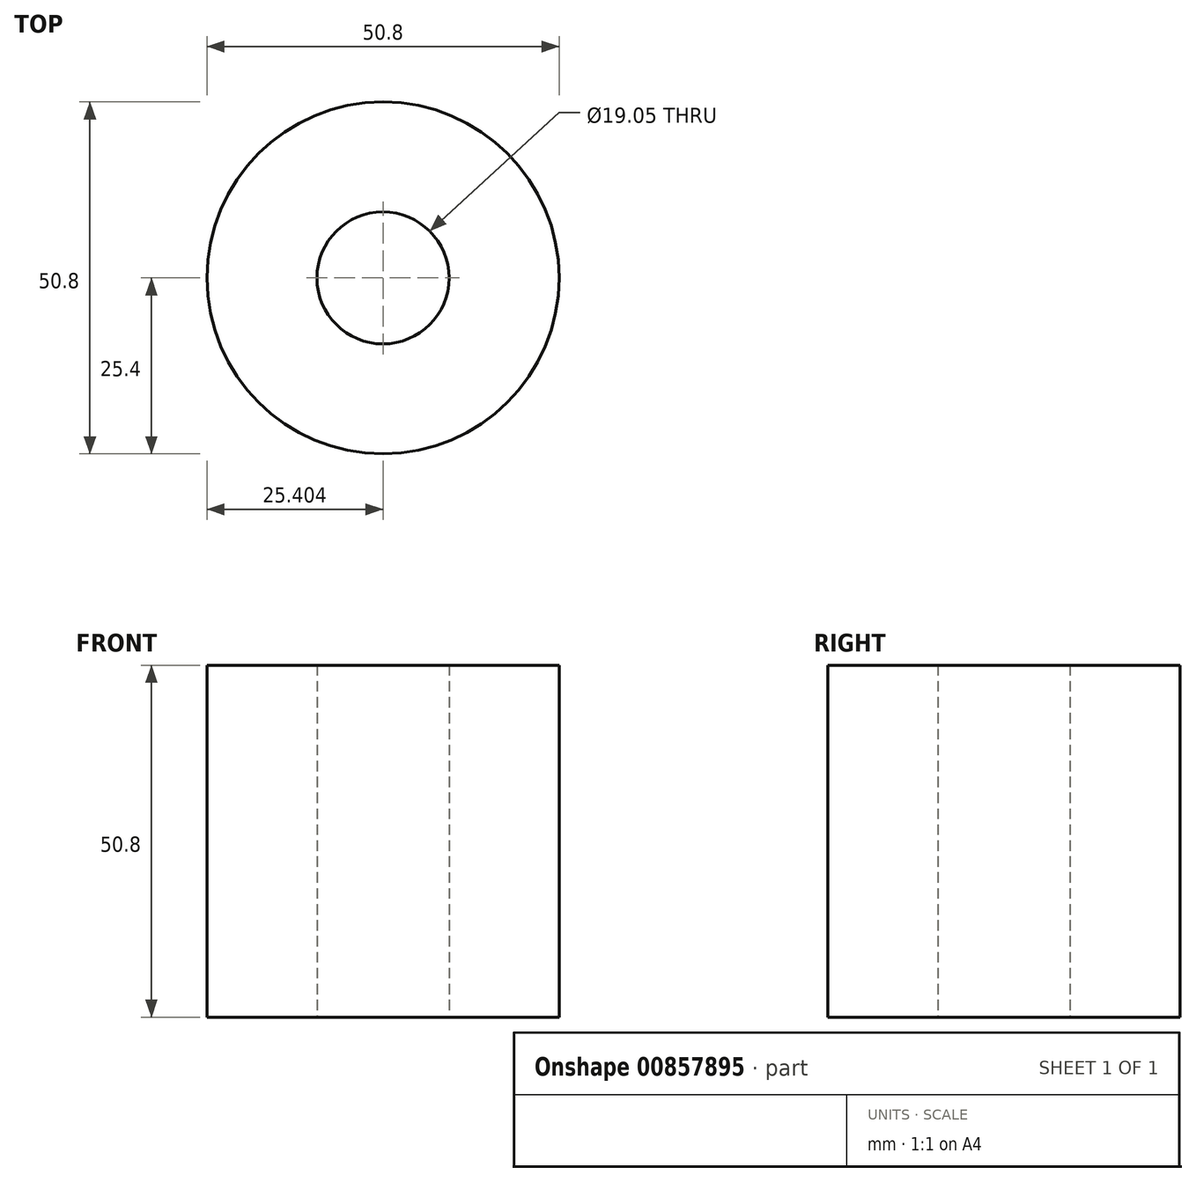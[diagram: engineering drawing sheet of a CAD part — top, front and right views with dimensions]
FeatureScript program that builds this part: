
annotation { "Feature Type Name" : "Feature", "Feature Type Description" : "" }
export const myFeature = defineFeature(function(context is Context, id is Id, definition is map)
    precondition{}
    {
        {
            var Q0;
            Q0=qCreatedBy(makeId("Top.planeOp"),FACE);
            var sketch = newSketch(context, id + "F0", { "sketchPlane" : qUnion([Q0])});
            skCircle(sketch, "E0", {"center": v(2.3, 0) * mm, "radius": 25.4 * mm});
            skCircle(sketch, "E1", {"center": v(2.3, 0) * mm, "radius": 9.53 * mm});
            skSolve(sketch);
        }
        {
            var Q0;
            Q0 = qSketchRegion(id + "F0", true);
            extrude(context, id + "F1", {"entities" : qUnion([Q0]), "depth" : 50.8 * mm, "offsetDistance" : 25.4 * mm});
        }
    });
